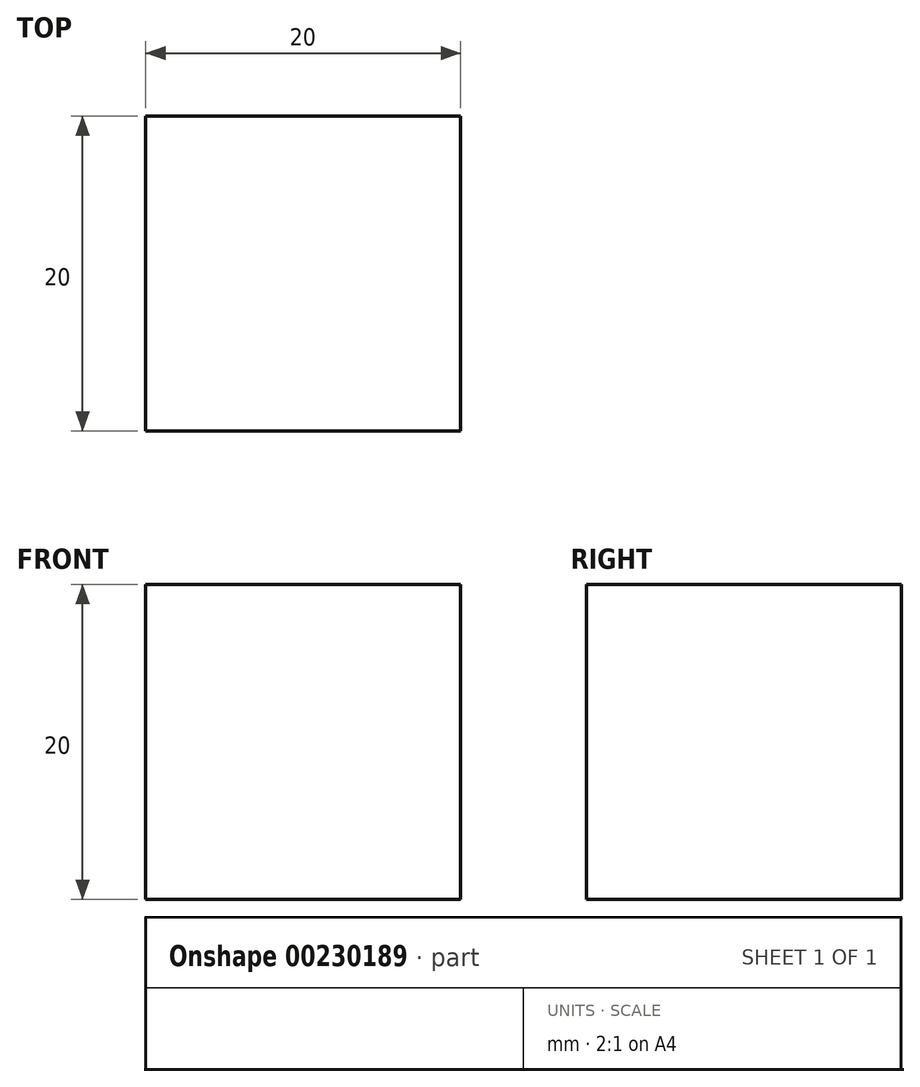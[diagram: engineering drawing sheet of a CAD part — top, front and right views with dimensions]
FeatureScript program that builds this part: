
annotation { "Feature Type Name" : "Feature", "Feature Type Description" : "" }
export const myFeature = defineFeature(function(context is Context, id is Id, definition is map)
    precondition{}
    {
        {
            var Q0;
            Q0=qCreatedBy(makeId("Top.planeOp"),FACE);
            var sketch = newSketch(context, id + "F0", { "sketchPlane" : qUnion([Q0])});
            skLineSegment(sketch, "E0", {"start": v(-20, 20) * mm, "end": v(-20, 0) * mm});
            skLineSegment(sketch, "E1", {"start": v(-20, 20) * mm, "end": v(0, 20) * mm});
            skLineSegment(sketch, "E2", {"start": v(-20, 0) * mm, "end": v(0, 0) * mm});
            skLineSegment(sketch, "E3", {"start": v(0, 0) * mm, "end": v(0, 20) * mm});
            skSolve(sketch);
        }
        {
            var Q0;
            Q0 = qSketchRegion(id + "F0", true);
            extrude(context, id + "F1", {"entities" : qUnion([Q0]), "depth" : 20 * mm});
        }
    });
